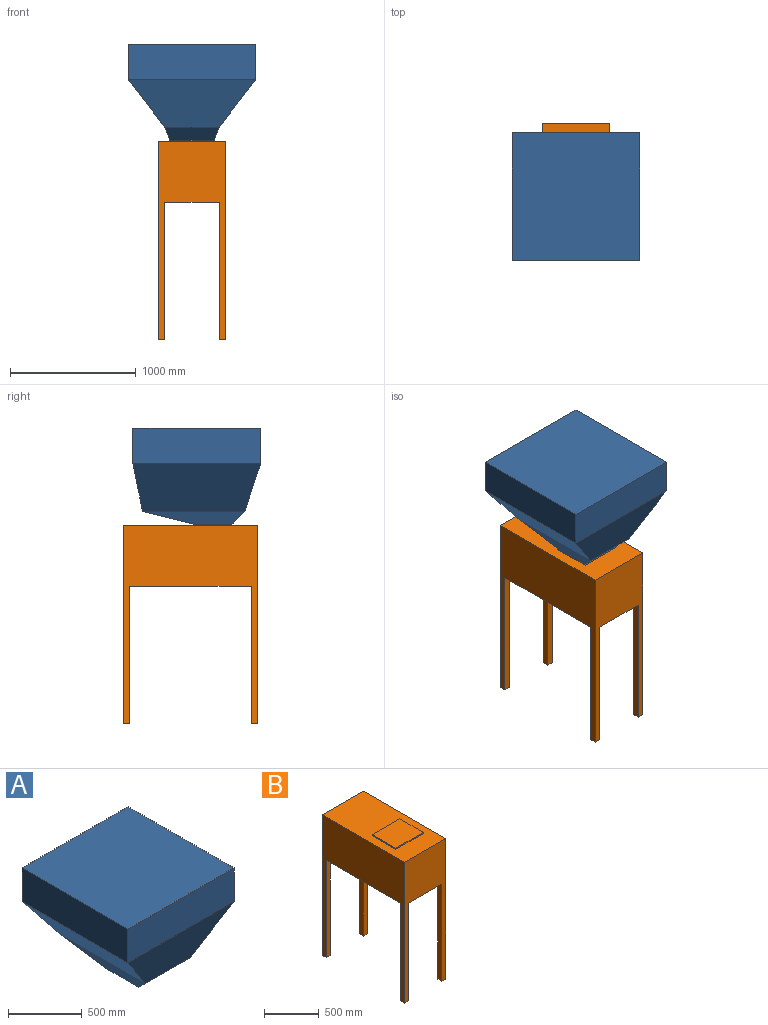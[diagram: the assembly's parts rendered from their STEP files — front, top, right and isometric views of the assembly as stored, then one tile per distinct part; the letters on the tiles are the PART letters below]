
ASSEMBLY  parts=2 mates=1
PART A: 14 faces, bbox 1016x1016x762 mm
  f0: plane 355.6x304.8mm, normal (0,0,-1), area 108386.9mm2, adj f1,f2,f3,f4
  f1: plane 431.8x406.4mm, normal (0,0.24,-0.97), area 164923.9mm2, adj f0,f2,f4,f6
  f2: plane 812.8x101.6mm, normal (-0.94,0,-0.35), area 60634.7mm2, adj f0,f1,f3,f7
  f3: plane 431.8x101.6mm, normal (0,-0.71,-0.71), area 56568.4mm2, adj f0,f2,f4,f8
  f4: plane 812.8x101.6mm, normal (0.94,0,-0.35), area 60634.7mm2, adj f0,f1,f3,f5
  f5: plane 1016x381mm, normal (0.79,0,-0.61), area 438991.4mm2, adj f4,f6,f8,f10
  f6: plane 1016x381mm, normal (0,0.98,-0.2), area 281267.9mm2, adj f1,f5,f7,f11
  f7: plane 1016x381mm, normal (-0.79,0,-0.61), area 438991.4mm2, adj f2,f6,f8,f12
  f8: plane 1016x381mm, normal (0,-0.95,-0.32), area 290724.9mm2, adj f3,f5,f7,f9
  f9: plane 1016x279.4mm, normal (0,-1,0), area 283870.4mm2, adj f8,f10,f12,f13
  f10: plane 1016x279.4mm, normal (1,0,0), area 283870.4mm2, adj f5,f9,f11,f13
  f11: plane 1016x279.4mm, normal (0,1,0), area 283870.4mm2, adj f6,f10,f12,f13
  f12: plane 1016x279.4mm, normal (-1,0,0), area 283870.4mm2, adj f7,f9,f11,f13
  f13: plane 1016x1016mm, normal (0,0,1), area 1032256mm2, adj f9,f10,f11,f12
PART B: 23 faces, bbox 533.4x1066.8x1587.5 mm
  f0: plane 1066.8x533.4mm, normal (0,0,1), area 460644.2mm2, adj f1,f2,f3,f4,f18,f19,f20,f21
  f1: plane 1574.8x1066.8mm, normal (1,0,0), area 625805.2mm2, adj f0,f2,f4,f5,f9,f11,f12,f14
  f2: plane 1574.8x533.4mm, normal (0,1,0), area 368386.4mm2, adj f0,f1,f3,f5,f13,f14,f16,f17
  f3: plane 1574.8x1066.8mm, normal (-1,0,0), area 625805.2mm2, adj f0,f2,f4,f5,f6,f8,f15,f17
  f4: plane 1574.8x533.4mm, normal (0,-1,0), area 368386.4mm2, adj f0,f1,f3,f5,f7,f8,f10,f11
  f5: plane 1066.8x533.4mm, normal (0,0,-1), area 558708.6mm2, adj f1,f2,f3,f4,f6,f7,f9,f10
  f6: plane 1092.2x50.8mm, normal (0,1,0), area 55483.8mm2, adj f3,f5,f7,f8
  f7: plane 1092.2x50.8mm, normal (1,0,0), area 55483.8mm2, adj f4,f5,f6,f8
  f8: plane 50.8x50.8mm, normal (0,0,-1), area 2580.6mm2, adj f3,f4,f6,f7
  f9: plane 1092.2x50.8mm, normal (0,1,0), area 55483.8mm2, adj f1,f5,f10,f11
  f10: plane 1092.2x50.8mm, normal (-1,0,0), area 55483.8mm2, adj f4,f5,f9,f11
  f11: plane 50.8x50.8mm, normal (0,0,-1), area 2580.6mm2, adj f1,f4,f9,f10
  f12: plane 1092.2x50.8mm, normal (0,-1,0), area 55483.8mm2, adj f1,f5,f13,f14
  f13: plane 1092.2x50.8mm, normal (-1,0,0), area 55483.8mm2, adj f2,f5,f12,f14
  f14: plane 50.8x50.8mm, normal (0,0,-1), area 2580.6mm2, adj f1,f2,f12,f13
  f15: plane 1092.2x50.8mm, normal (0,-1,0), area 55483.8mm2, adj f3,f5,f16,f17
  f16: plane 1092.2x50.8mm, normal (1,0,0), area 55483.8mm2, adj f2,f5,f15,f17
  f17: plane 50.8x50.8mm, normal (0,0,-1), area 2580.6mm2, adj f2,f3,f15,f16
  f18: plane 304.8x12.7mm, normal (-1,0,0), area 3871mm2, adj f0,f19,f21,f22
  f19: plane 355.6x12.7mm, normal (0,-1,0), area 4516.1mm2, adj f0,f18,f20,f22
  f20: plane 304.8x12.7mm, normal (1,0,0), area 3871mm2, adj f0,f19,f21,f22
  f21: plane 355.6x12.7mm, normal (0,1,0), area 4516.1mm2, adj f0,f18,f20,f22
  f22: plane 355.6x304.8mm, normal (0,0,1), area 108386.9mm2, adj f18,f19,f20,f21
PLACE A t=(0,-177.8,495.3)mm
PLACE B at identity fixed
MATE planar B.f22 <-> A.f0  axis (0,0,1) through (0,-177.8,495.3)mm
